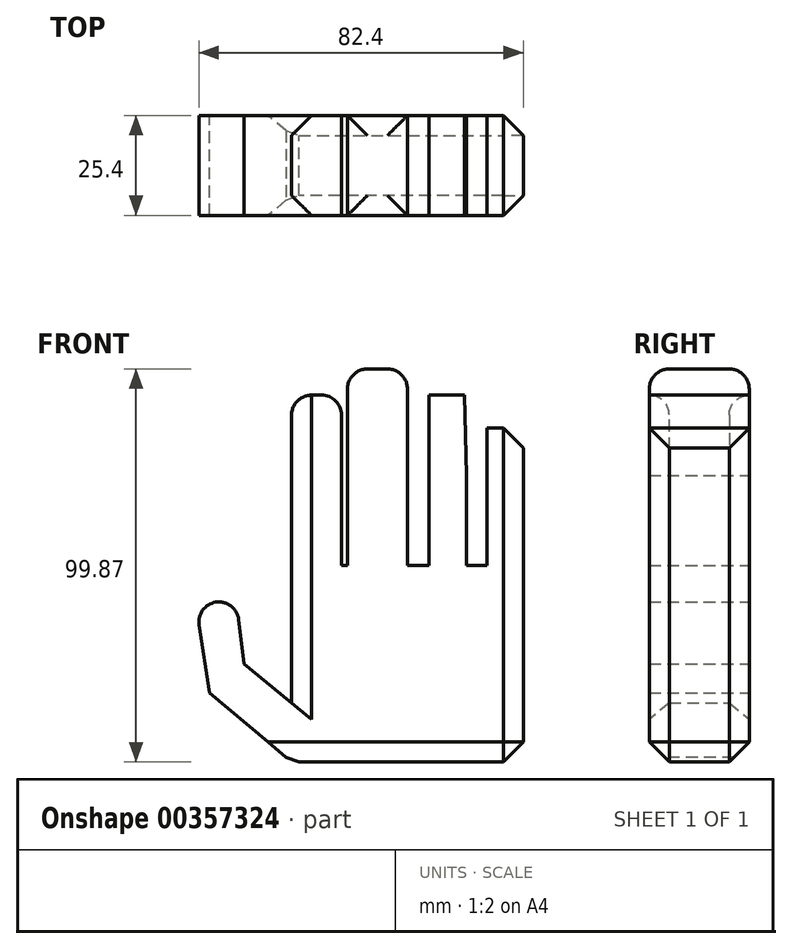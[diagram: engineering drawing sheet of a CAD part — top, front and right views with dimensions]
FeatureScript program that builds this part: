
annotation { "Feature Type Name" : "Feature", "Feature Type Description" : "" }
export const myFeature = defineFeature(function(context is Context, id is Id, definition is map)
    precondition{}
    {
        {
            var Q0;
            Q0=qCreatedBy(makeId("Front.planeOp"),FACE);
            var sketch = newSketch(context, id + "F0", { "sketchPlane" : qUnion([Q0])});
            skLineSegment(sketch, "E0.bottom", {"start": v(-29.44, 24.97) * mm, "end": v(29.44, 24.97) * mm});
            skLineSegment(sketch, "E0.top", {"start": v(-29.44, -24.97) * mm, "end": v(29.44, -24.97) * mm});
            skLineSegment(sketch, "E0.left", {"start": v(-29.44, 24.97) * mm, "end": v(-29.44, -24.97) * mm});
            skLineSegment(sketch, "E0.right", {"start": v(29.44, 24.97) * mm, "end": v(29.44, -24.97) * mm});
            skPoint(sketch, "E0.middle", {"position": v(0, 0) * mm});
            skLineSegment(sketch, "E1", {"start": v(-29.44, -24.97) * mm, "end": v(-50.22, -7.36) * mm});
            skLineSegment(sketch, "E2", {"start": v(-50.22, -7.36) * mm, "end": v(-41.56, 0) * mm});
            skLineSegment(sketch, "E3", {"start": v(-41.56, 0) * mm, "end": v(-29.44, -9.96) * mm});
            skLineSegment(sketch, "E4", {"start": v(-50.22, -7.36) * mm, "end": v(-53.69, 14.86) * mm});
            skLineSegment(sketch, "E5", {"start": v(-53.69, 14.86) * mm, "end": v(-43.5, 16.45) * mm});
            skLineSegment(sketch, "E6", {"start": v(-43.5, 16.45) * mm, "end": v(-41.56, 0) * mm});
            skLineSegment(sketch, "E7", {"start": v(-29.44, 24.97) * mm, "end": v(-29.44, 45.17) * mm});
            skLineSegment(sketch, "E8", {"start": v(-29.44, 45.17) * mm, "end": v(-16.74, 45.17) * mm});
            skLineSegment(sketch, "E9", {"start": v(-16.74, 45.17) * mm, "end": v(-16.74, 24.97) * mm});
            skLineSegment(sketch, "E10", {"start": v(-29.44, 45.17) * mm, "end": v(-29.44, 68.26) * mm});
            skLineSegment(sketch, "E11", {"start": v(-29.44, 68.26) * mm, "end": v(-16.74, 68.26) * mm});
            skLineSegment(sketch, "E12", {"start": v(-16.74, 68.26) * mm, "end": v(-16.74, 45.17) * mm});
            skLineSegment(sketch, "E13", {"start": v(-15.24, 24.97) * mm, "end": v(-15.24, 47.83) * mm});
            skLineSegment(sketch, "E14", {"start": v(-15.24, 47.83) * mm, "end": v(0, 47.83) * mm});
            skLineSegment(sketch, "E15", {"start": v(0, 47.83) * mm, "end": v(0, 24.97) * mm});
            skLineSegment(sketch, "E16", {"start": v(-15.24, 47.83) * mm, "end": v(-15.24, 74.9) * mm});
            skLineSegment(sketch, "E17", {"start": v(-15.24, 74.9) * mm, "end": v(0, 74.9) * mm});
            skLineSegment(sketch, "E18", {"start": v(0, 74.9) * mm, "end": v(0, 47.83) * mm});
            skLineSegment(sketch, "E19", {"start": v(5.48, 24.97) * mm, "end": v(5.48, 47.83) * mm});
            skLineSegment(sketch, "E20", {"start": v(5.48, 47.83) * mm, "end": v(15, 47.83) * mm});
            skLineSegment(sketch, "E21", {"start": v(15, 47.83) * mm, "end": v(15, 24.97) * mm});
            skLineSegment(sketch, "E22", {"start": v(5.48, 47.83) * mm, "end": v(5.48, 68.32) * mm});
            skLineSegment(sketch, "E23", {"start": v(5.48, 68.32) * mm, "end": v(14.43, 68.32) * mm});
            skLineSegment(sketch, "E24", {"start": v(14.43, 68.32) * mm, "end": v(15, 47.83) * mm});
            skLineSegment(sketch, "E25", {"start": v(29.44, 24.97) * mm, "end": v(29.44, 44.88) * mm});
            skLineSegment(sketch, "E26", {"start": v(29.44, 44.88) * mm, "end": v(20.2, 44.88) * mm});
            skLineSegment(sketch, "E27", {"start": v(20.2, 44.88) * mm, "end": v(20.2, 24.97) * mm});
            skLineSegment(sketch, "E28", {"start": v(20.2, 24.97) * mm, "end": v(20.2, 44.88) * mm});
            skLineSegment(sketch, "E29", {"start": v(20.2, 59.9) * mm, "end": v(29.44, 59.9) * mm});
            skLineSegment(sketch, "E30", {"start": v(29.44, 59.9) * mm, "end": v(29.44, 44.88) * mm});
            skLineSegment(sketch, "E31", {"start": v(20.2, 44.88) * mm, "end": v(20.2, 59.9) * mm});
            skSolve(sketch);
        }
        {
            var Q0;
            Q0 = qSketchRegion(id + "F0", true);
            extrude(context, id + "F1", {"entities" : qUnion([Q0]), "endBound" : BoundingType.SYMMETRIC, "depth" : 25.4 * mm});
        }
        {
            var Q0;
            Q0=makeQuery(id+"F1.opExtrude","SWEPT_EDGE",EDGE,{"disambiguationData":[OSD([sQuery(id+"F0.wireOp",EDGE,"E0.top"),sQuery(id+"F0.wireOp",EDGE,"E0.right")])]});
            var Q1;
            Q1=makeQuery(id+"F1.opExtrude","SWEPT_FACE",FACE,{"disambiguationData":[OSD([sQuery(id+"F0.wireOp",EDGE,"E0.right"),sQuery(id+"F0.wireOp",EDGE,"E25"),sQuery(id+"F0.wireOp",EDGE,"E30")])]});
            var Q2;
            Q2=makeQuery(id+"F1.opExtrude","CAP_EDGE",EDGE,{"disambiguationData":[OSD([sQuery(id+"F0.wireOp",EDGE,"E0.left"),sQuery(id+"F0.wireOp",EDGE,"E7"),sQuery(id+"F0.wireOp",EDGE,"E10")])],"isStart":false});
            var Q3;
            Q3=makeQuery(id+"F1.opExtrude","CAP_EDGE",EDGE,{"disambiguationData":[OSD([sQuery(id+"F0.wireOp",EDGE,"E0.left"),sQuery(id+"F0.wireOp",EDGE,"E7"),sQuery(id+"F0.wireOp",EDGE,"E10")])],"isStart":true});
            var Q4;
            Q4=makeQuery(id+"F1.opExtrude","CAP_EDGE",EDGE,{"disambiguationData":[OSD([sQuery(id+"F0.wireOp",EDGE,"E0.top")])],"isStart":true});
            var Q5;
            Q5=makeQuery(id+"F1.opExtrude","CAP_EDGE",EDGE,{"disambiguationData":[OSD([sQuery(id+"F0.wireOp",EDGE,"E0.top")])],"isStart":false});
            var Q6;
            Q6=makeQuery(id+"F1.opExtrude","SWEPT_EDGE",EDGE,{"disambiguationData":[OSD([sQuery(id+"F0.wireOp",EDGE,"E0.top"),sQuery(id+"F0.wireOp",EDGE,"E0.left"),sQuery(id+"F0.wireOp",EDGE,"E1")])]});
            chamfer(context, id + "F2", {"entities" : qUnion([Q0, Q1, Q2, Q3, Q4, Q5, Q6]), "width" : 5.08 * mm, "tangentPropagation" : true});
        }
        {
            var Q0;
            Q0=makeQuery(id+"F1.opExtrude","SWEPT_EDGE",EDGE,{"disambiguationData":[OSD([sQuery(id+"F0.wireOp",EDGE,"E4"),sQuery(id+"F0.wireOp",EDGE,"E5")])]});
            var Q1;
            Q1=makeQuery(id+"F1.opExtrude","SWEPT_EDGE",EDGE,{"disambiguationData":[OSD([sQuery(id+"F0.wireOp",EDGE,"E5"),sQuery(id+"F0.wireOp",EDGE,"E6")])]});
            var Q2;
            Q2=makeQuery(id+"F1.opExtrude","SWEPT_EDGE",EDGE,{"disambiguationData":[OSD([sQuery(id+"F0.wireOp",EDGE,"E10"),sQuery(id+"F0.wireOp",EDGE,"E11")])]});
            var Q3;
            Q3=makeQuery(id+"F1.opExtrude","SWEPT_EDGE",EDGE,{"disambiguationData":[OSD([sQuery(id+"F0.wireOp",EDGE,"E11"),sQuery(id+"F0.wireOp",EDGE,"E12")])]});
            var Q4;
            Q4=makeQuery(id+"F1.opExtrude","SWEPT_EDGE",EDGE,{"disambiguationData":[OSD([sQuery(id+"F0.wireOp",EDGE,"E16"),sQuery(id+"F0.wireOp",EDGE,"E17")])]});
            var Q5;
            Q5=makeQuery(id+"F1.opExtrude","SWEPT_FACE",FACE,{"disambiguationData":[OSD([sQuery(id+"F0.wireOp",EDGE,"E17")])]});
            fillet(context, id + "F3", {"entities" : qUnion([Q0, Q1, Q2, Q3, Q4, Q5]), "radius" : 5.08 * mm, "tangentPropagation" : true, "allowEdgeOverflow" : false});
        }
    });
